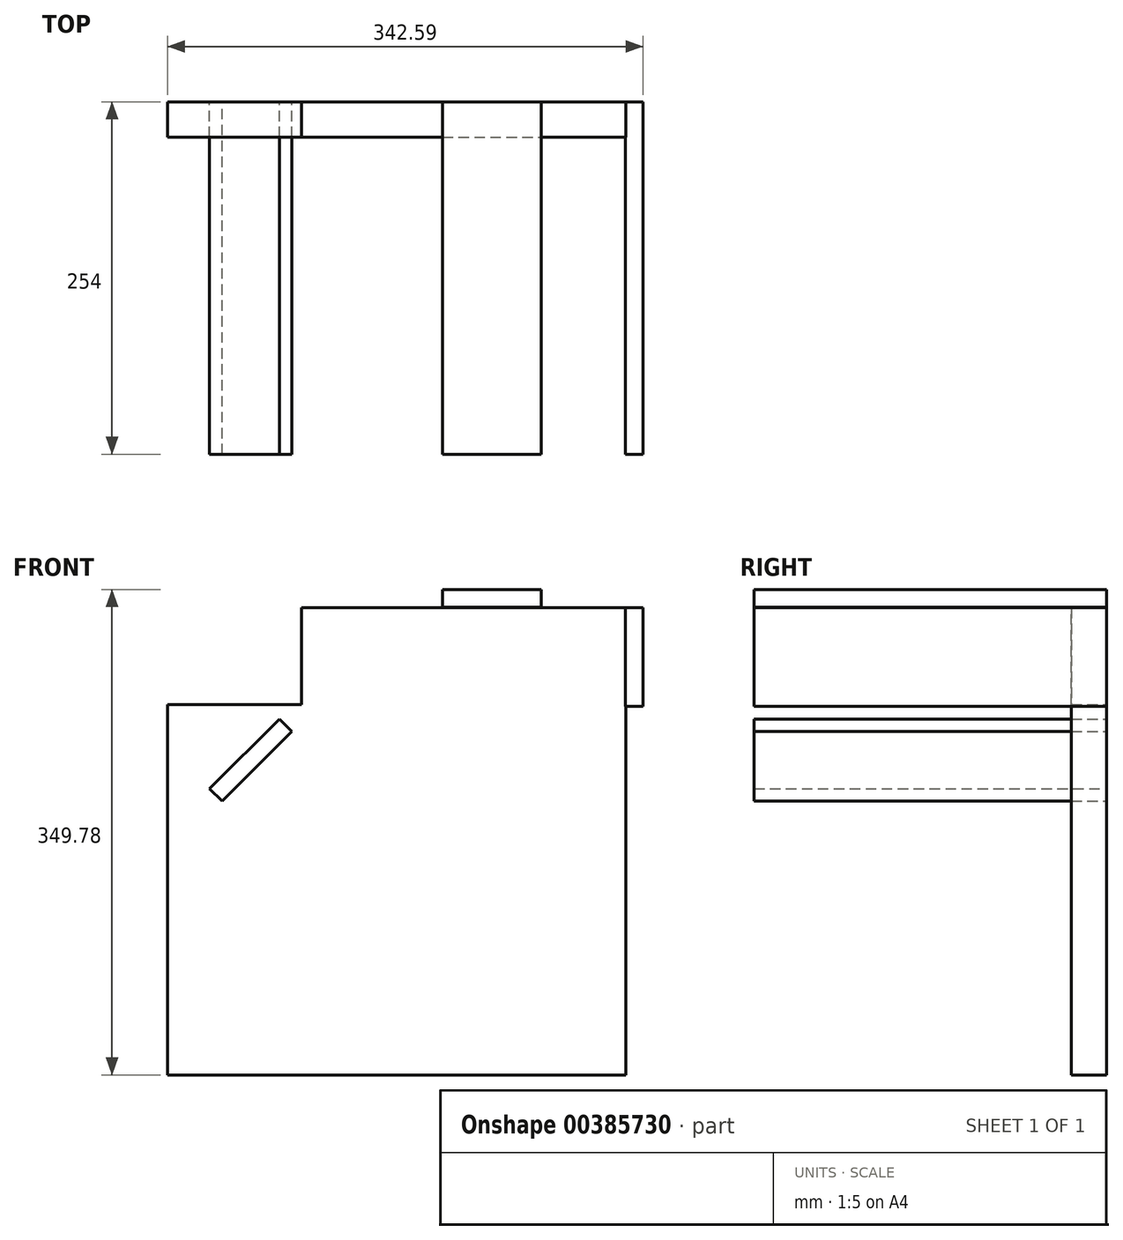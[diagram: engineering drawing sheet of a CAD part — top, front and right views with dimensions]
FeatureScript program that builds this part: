
annotation { "Feature Type Name" : "Feature", "Feature Type Description" : "" }
export const myFeature = defineFeature(function(context is Context, id is Id, definition is map)
    precondition{}
    {
        {
            var Q0;
            Q0=qCreatedBy(makeId("Front.planeOp"),FACE);
            var sketch = newSketch(context, id + "F0", { "sketchPlane" : qUnion([Q0])});
            skLineSegment(sketch, "E0", {"start": v(104.64, 101.6) * mm, "end": v(104.64, -162.56) * mm});
            skLineSegment(sketch, "E1", {"start": v(104.64, -162.56) * mm, "end": v(-225.56, -162.56) * mm});
            skLineSegment(sketch, "E2", {"start": v(-225.56, -162.56) * mm, "end": v(-225.56, 0) * mm});
            skLineSegment(sketch, "E3", {"start": v(-225.56, 0) * mm, "end": v(-129.04, 104.48) * mm});
            skLineSegment(sketch, "E4", {"start": v(-129.04, 104.48) * mm, "end": v(-129.04, 174.33) * mm});
            skLineSegment(sketch, "E5", {"start": v(-129.04, 174.33) * mm, "end": v(-27.44, 174.33) * mm});
            skLineSegment(sketch, "E6", {"start": v(-27.44, 174.33) * mm, "end": v(43.68, 174.33) * mm});
            skLineSegment(sketch, "E7", {"start": v(43.68, 174.33) * mm, "end": v(104.64, 174.33) * mm});
            skLineSegment(sketch, "E8", {"start": v(104.64, 101.6) * mm, "end": v(104.64, 174.33) * mm});
            skLineSegment(sketch, "E9", {"start": v(-129.04, 104.48) * mm, "end": v(-225.56, 104.48) * mm});
            skLineSegment(sketch, "E10", {"start": v(-225.56, 104.48) * mm, "end": v(-225.56, 0) * mm});
            skSolve(sketch);
        }
        {
            var Q0;
            Q0 = qSketchRegion(id + "F0", true);
            extrude(context, id + "F1", {"entities" : qUnion([Q0]), "depth" : 25.4 * mm});
        }
        {
            var Q0;
            Q0=qCreatedBy(makeId("Front.planeOp"),FACE);
            var sketch = newSketch(context, id + "F2", { "sketchPlane" : qUnion([Q0])});
            skLineSegment(sketch, "E11", {"start": v(-27.4, 174.52) * mm, "end": v(43.71, 174.52) * mm});
            skLineSegment(sketch, "E12", {"start": v(43.71, 174.52) * mm, "end": v(43.71, 187.22) * mm});
            skLineSegment(sketch, "E13", {"start": v(43.71, 187.22) * mm, "end": v(-27.4, 187.22) * mm});
            skLineSegment(sketch, "E14", {"start": v(-27.4, 187.22) * mm, "end": v(-27.4, 174.52) * mm});
            skLineSegment(sketch, "E15", {"start": v(104.33, 174.13) * mm, "end": v(104.33, 103.01) * mm});
            skLineSegment(sketch, "E16", {"start": v(104.33, 103.01) * mm, "end": v(117.03, 103.01) * mm});
            skLineSegment(sketch, "E17", {"start": v(117.03, 103.01) * mm, "end": v(117.03, 174.13) * mm});
            skLineSegment(sketch, "E18", {"start": v(117.03, 174.13) * mm, "end": v(104.33, 174.13) * mm});
            skLineSegment(sketch, "E19", {"start": v(-186.28, 34.67) * mm, "end": v(-136, 84.95) * mm});
            skLineSegment(sketch, "E20", {"start": v(-136, 84.95) * mm, "end": v(-144.97, 93.94) * mm});
            skLineSegment(sketch, "E21", {"start": v(-144.97, 93.94) * mm, "end": v(-195.26, 43.65) * mm});
            skLineSegment(sketch, "E22", {"start": v(-195.26, 43.65) * mm, "end": v(-186.28, 34.67) * mm});
            skSolve(sketch);
        }
        {
            var Q0;
            Q0 = qSketchRegion(id + "F2", true);
            extrude(context, id + "F3", {"entities" : qUnion([Q0]), "depth" : 254 * mm});
        }
        {
            var Q0;
            Q0=qCreatedBy(makeId("Front.planeOp"),FACE);
            var sketch = newSketch(context, id + "F4", { "sketchPlane" : qUnion([Q0])});
            skLineSegment(sketch, "E23", {"start": v(-217.98, 9.17) * mm, "end": v(-200.33, 27.44) * mm});
            skLineSegment(sketch, "E24", {"start": v(-200.33, 27.44) * mm, "end": v(-205.81, 32.74) * mm});
            skLineSegment(sketch, "E25", {"start": v(-205.81, 32.74) * mm, "end": v(-223.46, 14.46) * mm});
            skLineSegment(sketch, "E26", {"start": v(-223.46, 14.46) * mm, "end": v(-217.98, 9.17) * mm});
            skSolve(sketch);
        }
        {
            var Q0;
            Q0 = qSketchRegion(id + "F4", true);
            extrude(context, id + "F5", {"entities" : qUnion([Q0]), "operationType" : NewBodyOperationType.ADD, "depth" : 25.4 * mm});
        }
    });
